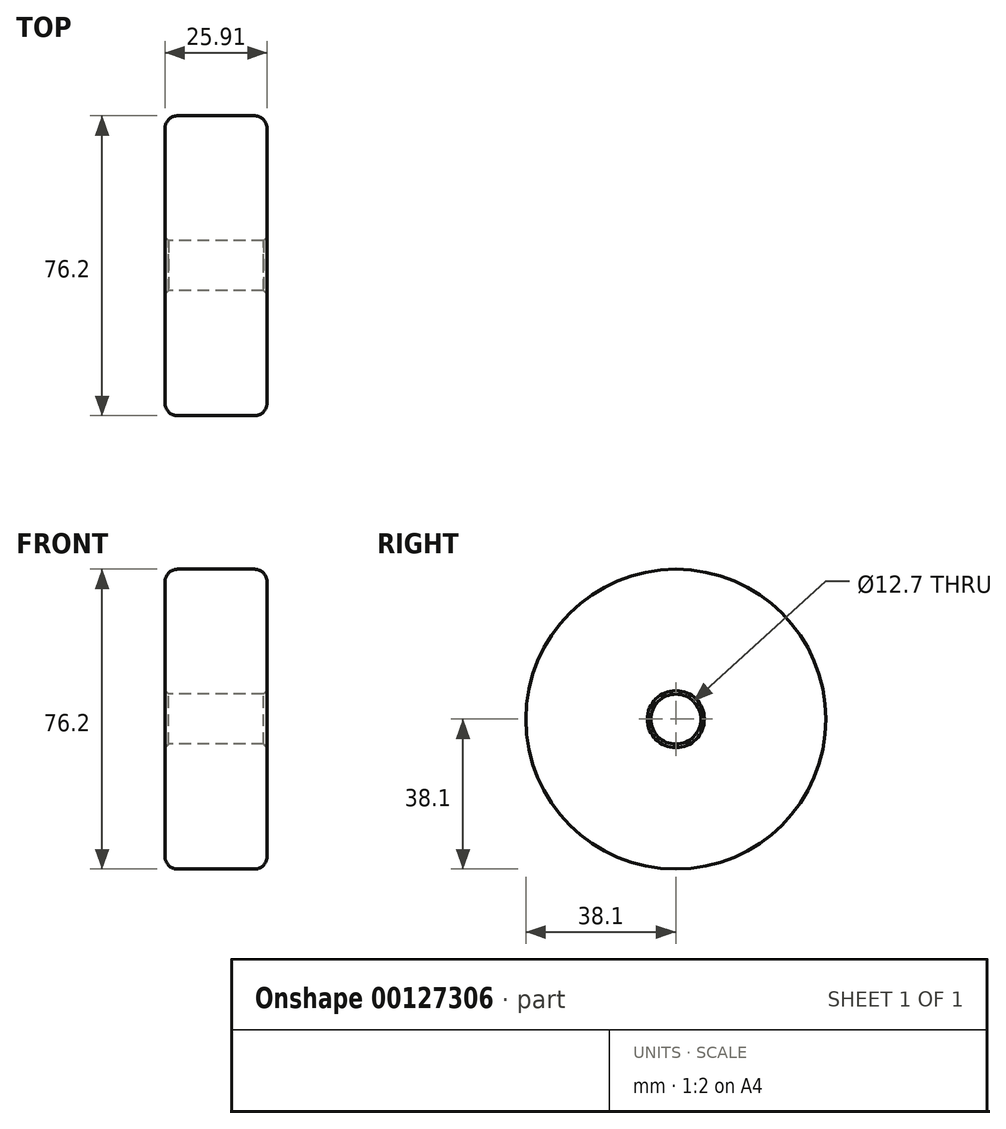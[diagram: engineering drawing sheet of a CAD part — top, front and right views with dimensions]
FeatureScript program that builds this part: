
annotation { "Feature Type Name" : "Feature", "Feature Type Description" : "" }
export const myFeature = defineFeature(function(context is Context, id is Id, definition is map)
    precondition{}
    {
        {
            var Q0;
            Q0=qCreatedBy(makeId("Right.planeOp"),FACE);
            var sketch = newSketch(context, id + "F0", { "sketchPlane" : qUnion([Q0])});
            skCircle(sketch, "E0", {"center": v(0, 0) * mm, "radius": 38.1 * mm});
            skCircle(sketch, "E1", {"center": v(0, 0) * mm, "radius": 6.35 * mm});
            skSolve(sketch);
        }
        {
            var Q0;
            Q0 = qSketchRegion(id + "F0", true);
            extrude(context, id + "F1", {"entities" : qUnion([Q0]), "depth" : 25.9 * mm});
        }
        {
            var Q0;
            Q0=makeQuery(id+"F1.opExtrude","SWEPT_FACE",FACE,{"disambiguationData":[OSD([sQuery(id+"F0.wireOp",EDGE,"E0")])]});
            fillet(context, id + "F2", {"entities" : qUnion([Q0]), "radius" : 3.17 * mm, "tangentPropagation" : true, "allowEdgeOverflow" : false});
        }
        {
            var Q0;
            Q0=makeQuery(id+"F1.opExtrude","SWEPT_FACE",FACE,{"disambiguationData":[OSD([sQuery(id+"F0.wireOp",EDGE,"E1")])]});
            chamfer(context, id + "F3", {"entities" : qUnion([Q0]), "width" : 0.89 * mm, "tangentPropagation" : true});
        }
    });
